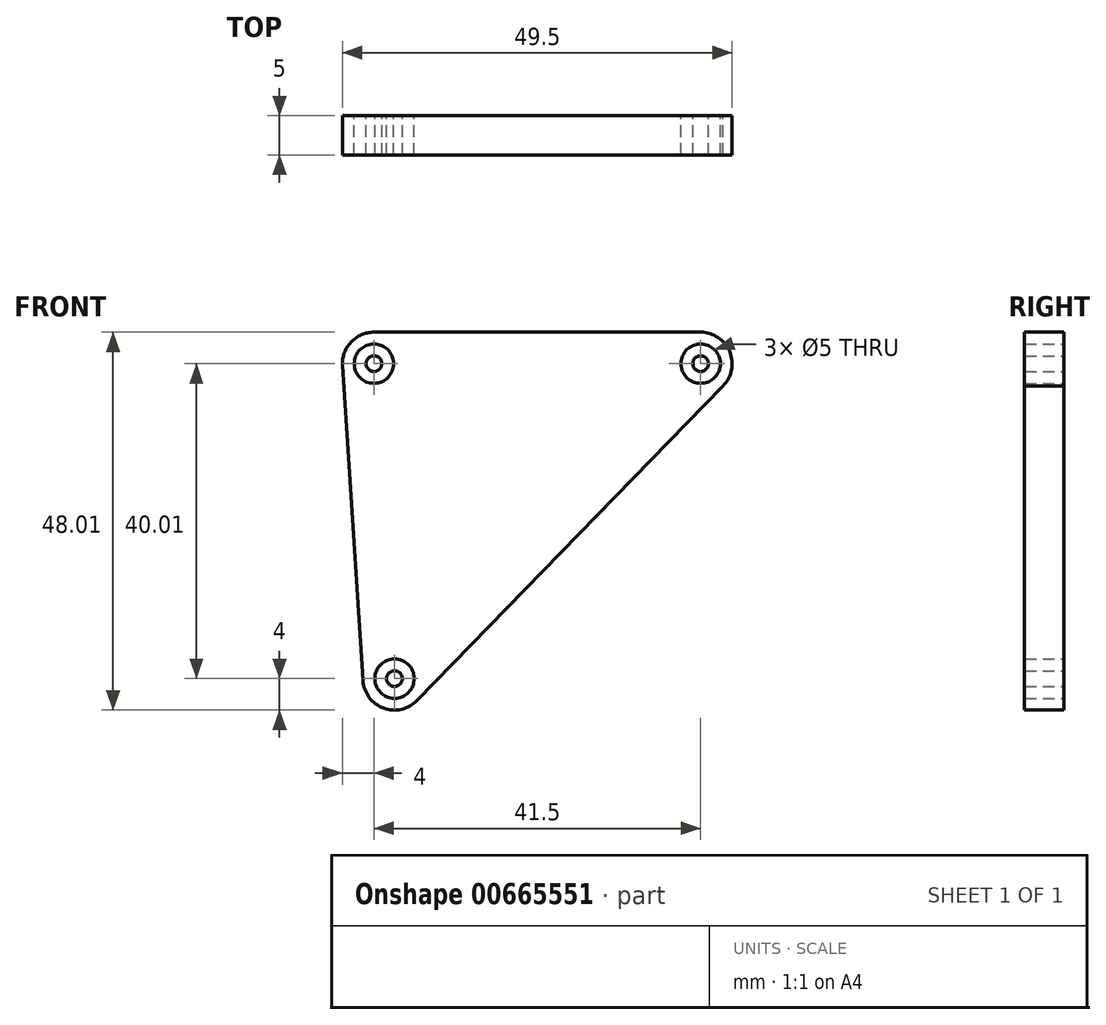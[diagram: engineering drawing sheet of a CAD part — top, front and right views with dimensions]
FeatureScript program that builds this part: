
annotation { "Feature Type Name" : "Feature", "Feature Type Description" : "" }
export const myFeature = defineFeature(function(context is Context, id is Id, definition is map)
    precondition{}
    {
        {
            var Q0;
            Q0=qCreatedBy(makeId("Front.planeOp"),FACE);
            var sketch = newSketch(context, id + "F0", { "sketchPlane" : qUnion([Q0])});
            skArc(sketch, "E0", {"start": v(-15.71, 6.74) * mm, "mid": v(-18.63, 5.47) * mm, "end": v(-19.7, 2.48) * mm});
            skArc(sketch, "E1", {"start": v(-17.1, -37.53) * mm, "mid": v(-14.48, -41.02) * mm, "end": v(-10.23, -40.06) * mm});
            skArc(sketch, "E2", {"start": v(28.61, -0.1) * mm, "mid": v(29.49, 4.27) * mm, "end": v(25.79, 6.74) * mm});
            skLineSegment(sketch, "E3", {"start": v(-19.7, 2.48) * mm, "end": v(-17.1, -37.53) * mm});
            skLineSegment(sketch, "E4", {"start": v(-15.71, 6.74) * mm, "end": v(25.79, 6.74) * mm});
            skLineSegment(sketch, "E5", {"start": v(28.7, 0) * mm, "end": v(-10.23, -40.06) * mm});
            skCircle(sketch, "E6", {"center": v(-15.71, 2.74) * mm, "radius": 2.5 * mm});
            skCircle(sketch, "E7", {"center": v(25.79, 2.74) * mm, "radius": 2.5 * mm});
            skCircle(sketch, "E8", {"center": v(-13.1, -37.27) * mm, "radius": 2.5 * mm});
            skCircle(sketch, "E9", {"center": v(-13.1, -37.27) * mm, "radius": 1 * mm});
            skCircle(sketch, "E10", {"center": v(25.79, 2.74) * mm, "radius": 1 * mm});
            skCircle(sketch, "E11", {"center": v(-15.71, 2.74) * mm, "radius": 1 * mm});
            skSolve(sketch);
        }
        {
            var Q0;
            Q0 = qSketchRegion(id + "F0", true);
            var Q1;
            Q1=makeQuery(id+"F0.imprint","IMPRINT",FACE,{"disambiguationData":[TD([[makeQuery(id+"F0.imprint","IMPRINT",EDGE,{"derivedFrom":sQuery(id+"F0.wireOp",EDGE,"E11")}),1.0]])]});
            var Q2;
            Q2=makeQuery(id+"F0.imprint","IMPRINT",FACE,{"disambiguationData":[TD([[makeQuery(id+"F0.imprint","IMPRINT",EDGE,{"derivedFrom":sQuery(id+"F0.wireOp",EDGE,"E9")}),1.0]])]});
            var Q3;
            Q3=makeQuery(id+"F0.imprint","IMPRINT",FACE,{"disambiguationData":[TD([[makeQuery(id+"F0.imprint","IMPRINT",EDGE,{"derivedFrom":sQuery(id+"F0.wireOp",EDGE,"E10")}),1.0]])]});
            extrude(context, id + "F1", {"entities" : qUnion([Q0, Q1, Q2, Q3]), "depth" : 5 * mm, "offsetDistance" : 25 * mm});
        }
    });
